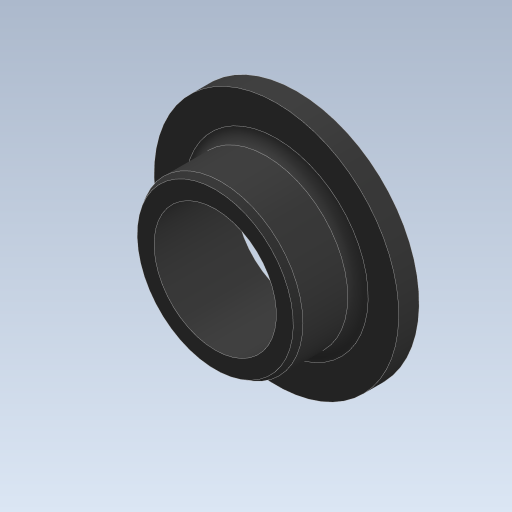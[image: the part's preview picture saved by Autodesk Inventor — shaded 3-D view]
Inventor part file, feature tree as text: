
AUTODESK INVENTOR PART (.ipt)
format: ipt  version: 2024 (Build 280153000, 153)  size: 150,528 bytes
history: native  units: mm
features: other x1, revolve x1, fillet x1, chamfer x1, sketch x1
ambient origin geometry x8: Origin, YZ Plane, XZ Plane, XY Plane, X Axis, Y Axis, Z Axis, Center Point
bodies: Body1 (feature_tree)
feature tree (5):
  other  "ソリッド1"
  revolve  "回転1"
  fillet  "フィレット1"  Radius=6.0mm
  chamfer  "面取り1"  Distance=8.0mm
  sketch  "スケッチ1"
